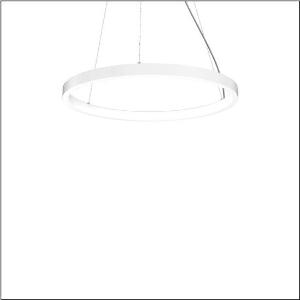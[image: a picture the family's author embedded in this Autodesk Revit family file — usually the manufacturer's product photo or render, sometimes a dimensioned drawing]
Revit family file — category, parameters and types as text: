
# Revit family: silica_r__21_ring-i_5pjbi3d3004a_ea64
name_source: partatom
category: Lighting Fixtures
units: mm (PartAtom-declared; Revit-internal decimal feet)

## family parameters
Cut with Voids When Loaded = No
Host = Face
Light Source = No
Part Type = Normal
Room Calculation Point = No
Round Connector Dimension = Use Diameter
Shared = No

## types (1)
- Silica® 21 Ring-I (1 x LED, 6430 lm, 105 W, 4000K)
    Apparent Load = 105 VA
    CIE Flux Codes = 22 48 76 50 101
    Color Rendering = 80
    Color Temperature = 4000K
    Default Elevation = 1800 mm
    Description = Silica® 21 Ring-I, suspended luminaire, of PMMA, frosted, light emission: inner ring side luminous distribution, primary light characteristic: symmetric, installation type: suspended mounting, LED, rated luminous flux: 6.430lm, luminous efficacy: 61lm/W, light colour: 840, colour temperature: 4000K, with terminal, 5-pole, mains connection: 230V, AC/DC, 0/50..60Hz, rated input power: 105W, housing, of extruded aluminium section, traffic white (RAL 9016), diameter: 1.090mm, ceiling canopy, traffic white (RAL 9016), protection rating (lamp compartment): IP40, insulation class (complete): insulation class I (protective earthing), certification: CE, impact resistance: IK02, permissible operating ambient temperature: 0..+35°C, packaging unit: 1 piece
    Height = 48 mm  [stored 0.15748 ft]
    Lamp = 1 x LED
    Lamp Light Flux = 6430 lm
    Lamp Power = 105 W
    Lamp count = 1
    Length = 1090 mm
    Luminous efficacy = 61 lm/W
    Manufacturer = Siteco
    ModVariant = No
    Model = 5PJBI3D3004A
    Mounting Place = Ceiling
    Mounting Type = Pendant
    Number of Poles = 1
    OnlyDefault = Yes
    Power Factor = 1
    Product Name = Silica® 21 Ring-I
    Product group = suspended luminaire
    ProductGroupID = 904
    Protection Class = Protection class I
    Protection Degree = Degree of protection
    RLX_Detail_Level = 1
    RLX_Emergency_Light_Flux = 0 lm
    RLX_Emergency_Type = 0
    RLX_Emergency_Type_DB = No
    RlxData = <blob elided: 12781 chars, md5=6a0e2c47>
    Socket = socket
    Standby Power = 0 W
    System Light Flux = 6430 lm
    System Power = 105 W
    Type Comments = Product without accessories
    Type Image = l_1258371.jpg
    URL = http://relux.com
    VarID = ---
    Voltage = 0 V
    Weight = 0.00 kg
    Width = 0 mm  [stored 0 ft]

note: [stored X ft] marks values corroborated as IEEE doubles in the binary element streams (Revit-internal decimal feet)

## geometry (parser evidence)
native form markers: Sweep x12
no freeform markers — native parametric forms only
